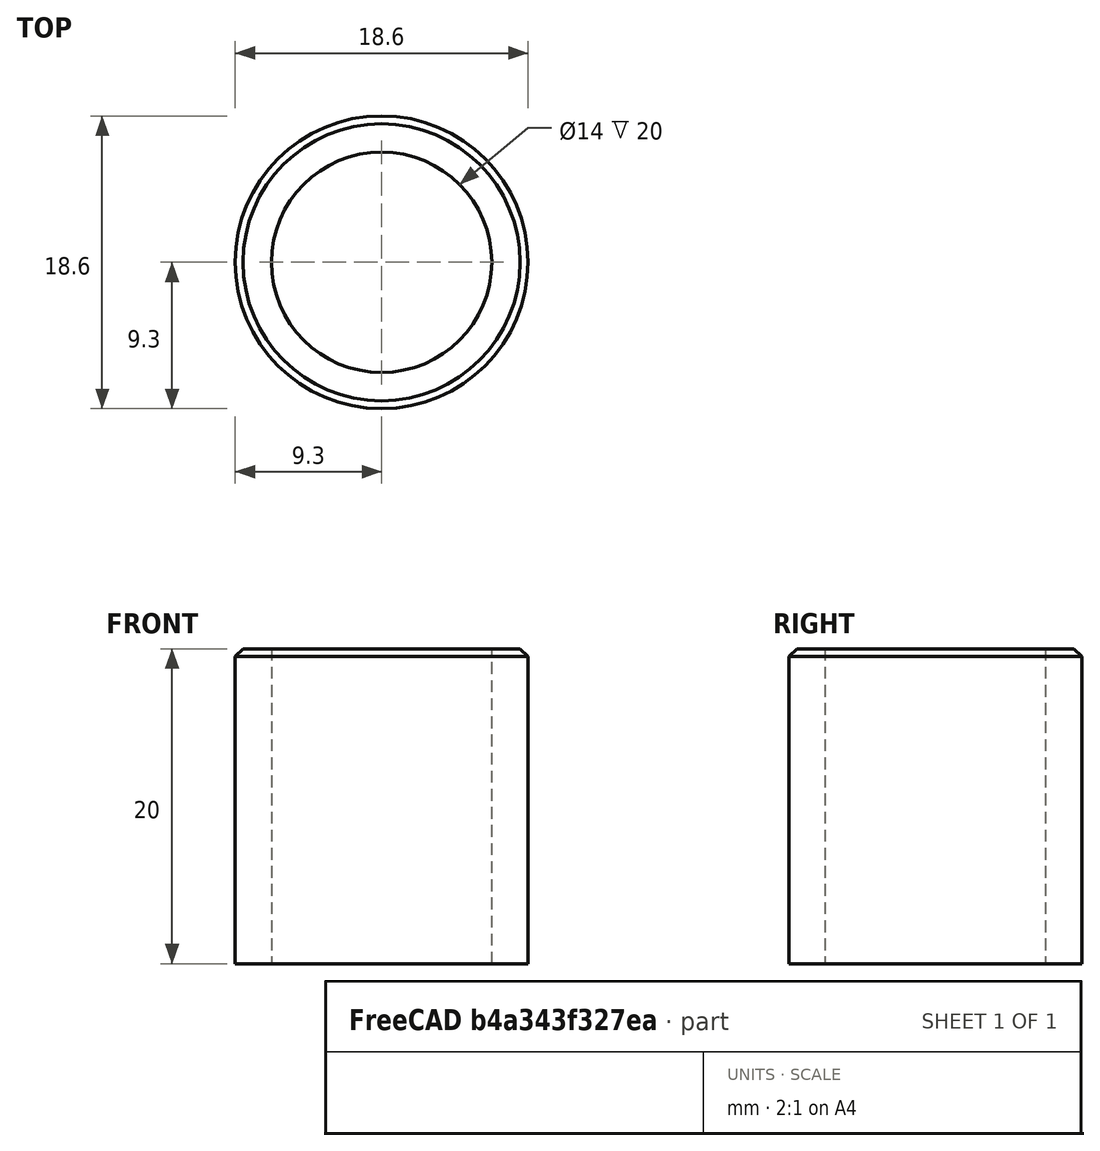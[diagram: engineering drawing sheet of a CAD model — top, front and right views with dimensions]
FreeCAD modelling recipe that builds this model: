
FCSTD DOCUMENT  (FreeCAD 0.19R24276 (Git))
Label: Tension_roller_v3_1_in_part
License: All rights reserved
LicenseURL: http://en.wikipedia.org/wiki/All_rights_reserved
objects: Sketcher::SketchObject×1, PartDesign::Pad×1, PartDesign::Chamfer×1, PartDesign::Body×1
note: 6 computed .brp shape members not serialized (recipe doc carries the construction recipe); baked Part::Feature solids carry a one-line shape summary decoded from their .brp

FEATURE [Sketcher::SketchObject] Sketch
  FullyConstrained = true
  MapMode = 5
  Support = -> [XY_Plane]
  sketch-geometry (2):
    g0: Circle CenterX=0 CenterY=0 CenterZ=0 NormalX=0 NormalY=0 NormalZ=1 AngleXU=0 Radius=7
    g1: Circle CenterX=0 CenterY=0 CenterZ=0 NormalX=0 NormalY=0 NormalZ=1 AngleXU=0 Radius=9.3
  constraints (4):
    c: Coincident(g0,g-1)
    c: Coincident(g1,g0)
    c: Diameter(g0) = 14
    c: Diameter(g1) = 18.6
FEATURE [PartDesign::Pad] Pad
  Direction = (1,1,1)
  Length = 20
  Length2 = 100
  Profile = -> Sketch
  Type = 0
FEATURE [PartDesign::Chamfer] Chamfer
  Angle = 45
  Base = -> Pad [Edge3]
  BaseFeature = -> Pad
  ChamferType = 0
  FlipDirection = false
  Size = 0.5
  Size2 = 1
  SupportTransform = false
FEATURE [PartDesign::Body] Body
  Group = -> [Sketch,Pad,Chamfer]
  Origin = -> Origin
  Tip = -> Chamfer
